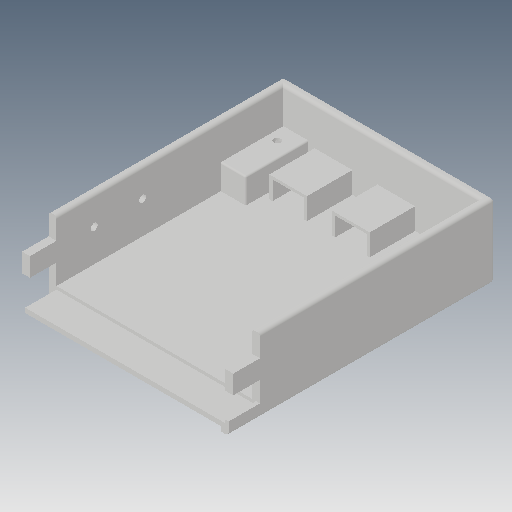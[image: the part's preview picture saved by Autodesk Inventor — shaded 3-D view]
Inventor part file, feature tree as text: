
AUTODESK INVENTOR PART (.ipt)
format: ipt  version: 2019 (Build 230136000, 136)  size: 409,600 bytes
history: native  units: mm
features: extrude x10, sketch x10, projected_geometry x5, other x5, fillet x2, plane x2, surface_op x1
ambient origin geometry x8: Origin, YZ Plane, XZ Plane, XY Plane, X Axis, Y Axis, Z Axis, Center Point
bodies: Solid1 (feature_tree)
feature tree (35):
  extrude  "Extrusion1"  Depth=170.0mm
  extrude  "Extrusion2"  Depth=5.0mm
  extrude  "Extrusion3"  Depth=25.0mm TaperAngle=0.0deg
  fillet  "Fillet1"  Radius=2.0mm
  extrude  "Extrusion4"  TaperAngle=0.0deg  [1 undecoded]
  extrude  "Extrusion5"  Depth=40.0mm
  fillet  "Fillet2"  [1 undecoded]
  plane  "Work Plane2"
  extrude  "Extrusion7"  Depth=35.0mm
  plane  "Work Plane1"
  extrude  "Extrusion8"  Depth=16.0mm TaperAngle=0.0deg
  surface_op  "Sculpt3"
  sketch  "Sketch8"  dims[d20=4.5mm d22=6.0mm]
  extrude  "Extrusion15"  Depth=6.0mm
  extrude  "Extrusion16"  Depth=7.0mm
  extrude  "Extrusion18"  Depth=1.0mm
  sketch  "Sketch1"  dims[d0=135.0mm d1=170.0mm]
  sketch  "Sketch2"  dims[d2=46.7mm d3=0.0mm d4=5.0mm]
  projected_geometry  "Projected Loop1"
  sketch  "Sketch3"  dims[d5=38.7mm d6=0.0mm d7=25.0mm d8=0.0mm d9=2.0mm]
  projected_geometry  "Projected Loop2"
  sketch  "Sketch4"  dims[d10=0.0mm d11=0.0mm]
  sketch  "Sketch5"  dims[d12=16.0mm d13=40.0mm d14=0.0mm]
  sketch  "Sketch6"  dims[d15=0.0mm d16=35.0mm]
  sketch  "Sketch7"  dims[d17=16.0mm d18=16.0mm d19=0.0mm]
  sketch  "Sketch14"  dims[d23=4.5mm d24=7.0mm]
  projected_geometry  "Projected Loop10"
  sketch  "Sketch16"  dims[d26=12.0mm d27=0.0mm d28=1.0mm d29=4.5mm d30=4.5mm d31=30.8mm d34=90.0mm d37=0.0mm d38=0.0mm d39=-1.5mm d40=7.5mm d41=7.5mm d42=3.15mm d43=0.0mm d44=10.0mm d45=12.5mm d46=18.0mm d51=20.0mm d70=1.75mm d91=12.0mm d92=8.0mm d93=2.05mm d94=2.05mm d95=20.0mm d96=29.0mm d97=0.0mm d98=0.8mm d99=0.8mm d100=1.8mm d101=4.4mm d102=0.0mm d105=1.8mm d106=4.4mm d107=0.0mm]
  projected_geometry  "Projected Loop13"
  projected_geometry  "Projected Loop14"
  other  "Composite3"
  other  "Srf3"
  parser-record x1  (decoder bookkeeping rows leaked as tree rows — omitted from the tree; the rows remain in map.json)
  other  "Case B.iam"
  other  "Case_B1:1"
note: 2 required parameter values undecoded (feature->parameter linkage not recoverable at this tier; creation-order binding heuristic only, values carry confidence <= 0.55)
note: 1 file-system path scrubbed to <path> (originals preserved in map.json)
